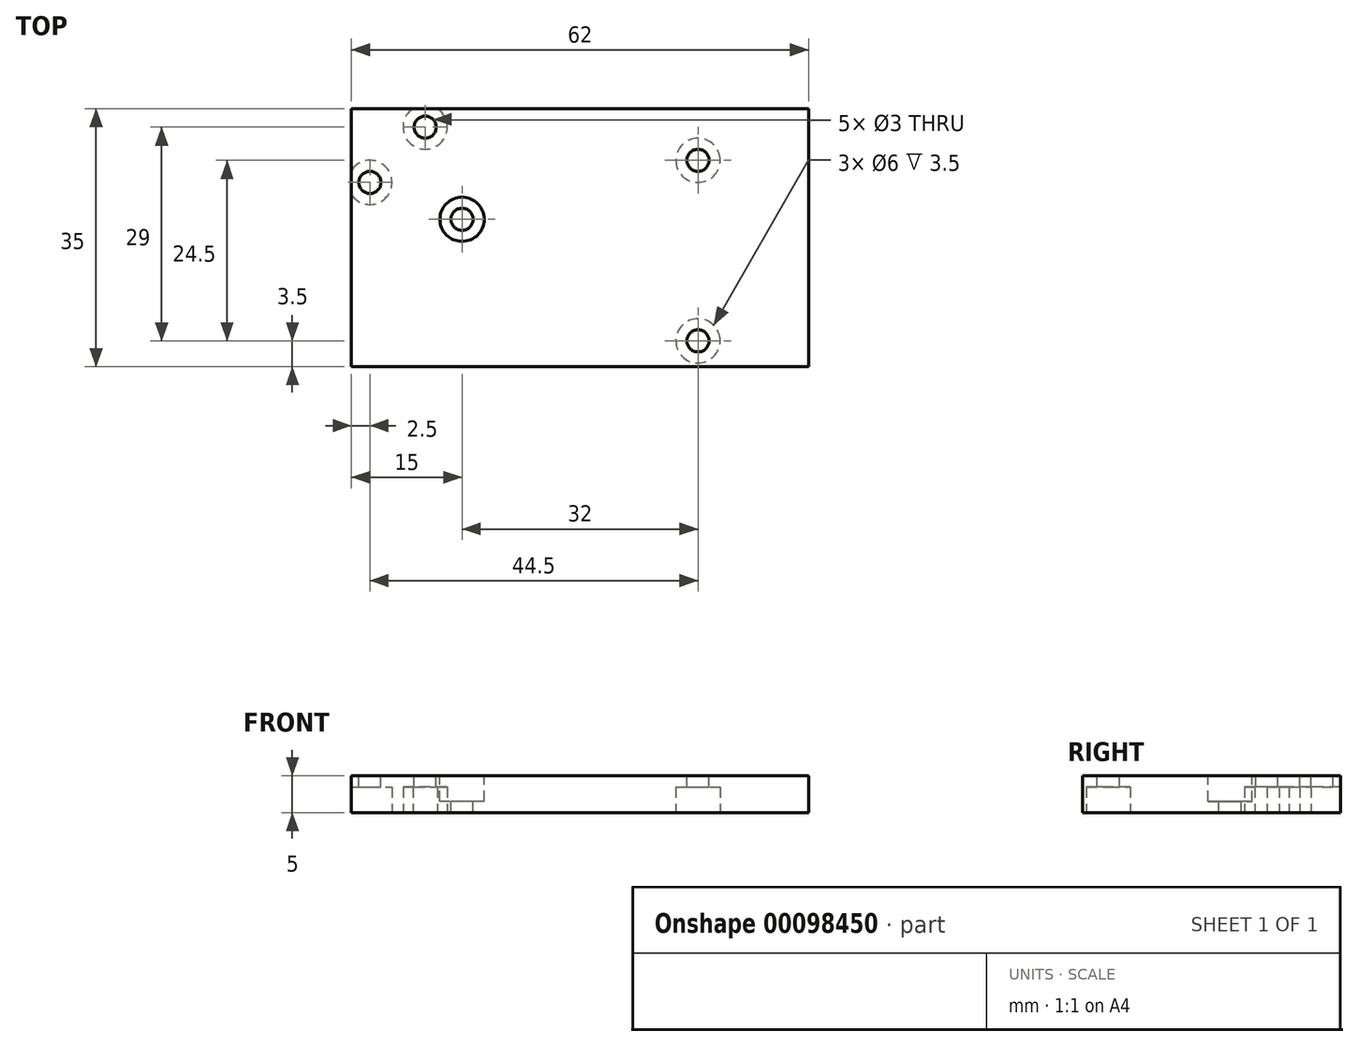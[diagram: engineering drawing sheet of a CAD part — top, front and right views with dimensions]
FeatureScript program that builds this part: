
annotation { "Feature Type Name" : "Feature", "Feature Type Description" : "" }
export const myFeature = defineFeature(function(context is Context, id is Id, definition is map)
    precondition{}
    {
        {
            var Q0;
            Q0=qCreatedBy(makeId("Top.planeOp"),FACE);
            var sketch = newSketch(context, id + "F0", { "sketchPlane" : qUnion([Q0])});
            skLineSegment(sketch, "E0.bottom", {"start": v(31, -17.5) * mm, "end": v(-31, -17.5) * mm});
            skLineSegment(sketch, "E0.top", {"start": v(31, 17.5) * mm, "end": v(-31, 17.5) * mm});
            skLineSegment(sketch, "E0.left", {"start": v(31, -17.5) * mm, "end": v(31, 17.5) * mm});
            skLineSegment(sketch, "E0.right", {"start": v(-31, -17.5) * mm, "end": v(-31, 17.5) * mm});
            skPoint(sketch, "E0.middle", {"position": v(0, 0) * mm});
            skSolve(sketch);
        }
        {
            var Q0;
            Q0=makeQuery(id+"F0.imprint","IMPRINT",FACE,{"disambiguationData":[TD([[makeQuery(id+"F0.imprint","IMPRINT",EDGE,{"derivedFrom":sQuery(id+"F0.wireOp",EDGE,"E0.bottom")}),-1.0]])]});
            extrude(context, id + "F1", {"entities" : qUnion([Q0]), "depth" : 5 * mm});
        }
        {
            var Q0;
            Q0=makeQuery(id+"F1.opExtrude","CAP_FACE",FACE,{"disambiguationData":[OSD([sQuery(id+"F0.wireOp",EDGE,"E0.bottom"),sQuery(id+"F0.wireOp",EDGE,"E0.top"),sQuery(id+"F0.wireOp",EDGE,"E0.left"),sQuery(id+"F0.wireOp",EDGE,"E0.right")])],"isStart":false});
            var sketch = newSketch(context, id + "F2", { "sketchPlane" : qUnion([Q0])});
            skCircle(sketch, "E1", {"center": v(-28.5, 7.5) * mm, "radius": 1.5 * mm});
            skCircle(sketch, "E2", {"center": v(-21, 15) * mm, "radius": 1.5 * mm});
            skSolve(sketch);
        }
        {
            var Q0;
            Q0 = qSketchRegion(id + "F2", true);
            extrude(context, id + "F3", {"entities" : qUnion([Q0]), "operationType" : NewBodyOperationType.REMOVE, "oppositeDirection" : true, "depth" : 5 * mm});
        }
        {
            var Q0;
            Q0=makeQuery(id+"F1.opExtrude","CAP_FACE",FACE,{"disambiguationData":[OSD([sQuery(id+"F0.wireOp",EDGE,"E0.bottom"),sQuery(id+"F0.wireOp",EDGE,"E0.top"),sQuery(id+"F0.wireOp",EDGE,"E0.left"),sQuery(id+"F0.wireOp",EDGE,"E0.right")])],"isStart":true});
            var sketch = newSketch(context, id + "F4", { "sketchPlane" : qUnion([Q0])});
            skCircle(sketch, "E3", {"center": v(-28.5, -7.5) * mm, "radius": 3 * mm});
            skCircle(sketch, "E4", {"center": v(-21, -15) * mm, "radius": 3 * mm});
            skSolve(sketch);
        }
        {
            var Q0;
            Q0 = qSketchRegion(id + "F4", true);
            extrude(context, id + "F5", {"entities" : qUnion([Q0]), "operationType" : NewBodyOperationType.REMOVE, "oppositeDirection" : true, "depth" : 3.5 * mm});
        }
        {
            var Q0;
            Q0=makeQuery(id+"F1.opExtrude","CAP_FACE",FACE,{"disambiguationData":[OSD([sQuery(id+"F0.wireOp",EDGE,"E0.bottom"),sQuery(id+"F0.wireOp",EDGE,"E0.top"),sQuery(id+"F0.wireOp",EDGE,"E0.left"),sQuery(id+"F0.wireOp",EDGE,"E0.right")])],"isStart":false});
            var sketch = newSketch(context, id + "F6", { "sketchPlane" : qUnion([Q0])});
            skCircle(sketch, "E5", {"center": v(-16, 2.5) * mm, "radius": 3 * mm});
            skSolve(sketch);
        }
        {
            var Q0;
            Q0=makeQuery(id+"F6.imprint","IMPRINT",FACE,{"disambiguationData":[TD([[makeQuery(id+"F6.imprint","IMPRINT",EDGE,{"derivedFrom":sQuery(id+"F6.wireOp",EDGE,"E5")}),1.0]])]});
            extrude(context, id + "F7", {"entities" : qUnion([Q0]), "operationType" : NewBodyOperationType.REMOVE, "oppositeDirection" : true, "depth" : 3.5 * mm});
        }
        {
            var Q0;
            Q0=makeQuery(id+"F7.boolean.opBoolean","COPY",FACE,{"derivedFrom":makeQuery(id+"F7.opExtrude","CAP_FACE",FACE,{"disambiguationData":[OSD([sQuery(id+"F6.wireOp",EDGE,"E5")])],"isStart":false})});
            var sketch = newSketch(context, id + "F8", { "sketchPlane" : qUnion([Q0])});
            skCircle(sketch, "E6", {"center": v(-16, 2.5) * mm, "radius": 1.5 * mm});
            skSolve(sketch);
        }
        {
            var Q0;
            Q0 = qSketchRegion(id + "F8", true);
            extrude(context, id + "F9", {"entities" : qUnion([Q0]), "operationType" : NewBodyOperationType.REMOVE, "oppositeDirection" : true, "depth" : 5 * mm});
        }
        {
            var Q0;
            Q0=makeQuery(id+"F1.opExtrude","CAP_FACE",FACE,{"disambiguationData":[OSD([sQuery(id+"F0.wireOp",EDGE,"E0.bottom"),sQuery(id+"F0.wireOp",EDGE,"E0.top"),sQuery(id+"F0.wireOp",EDGE,"E0.left"),sQuery(id+"F0.wireOp",EDGE,"E0.right")])],"isStart":false});
            var sketch = newSketch(context, id + "F10", { "sketchPlane" : qUnion([Q0])});
            skCircle(sketch, "E7", {"center": v(16, 10.5) * mm, "radius": 1.5 * mm});
            skCircle(sketch, "E8", {"center": v(16, -14) * mm, "radius": 1.5 * mm});
            skLineSegment(sketch, "E9", {"start": v(16, 10.5) * mm, "end": v(16, -14) * mm, "construction": true});
            skSolve(sketch);
        }
        {
            var Q0;
            Q0 = qSketchRegion(id + "F10", true);
            extrude(context, id + "F11", {"entities" : qUnion([Q0]), "operationType" : NewBodyOperationType.REMOVE, "oppositeDirection" : true, "depth" : 5 * mm});
        }
        {
            var Q0;
            Q0=makeQuery(id+"F1.opExtrude","CAP_FACE",FACE,{"disambiguationData":[OSD([sQuery(id+"F0.wireOp",EDGE,"E0.bottom"),sQuery(id+"F0.wireOp",EDGE,"E0.top"),sQuery(id+"F0.wireOp",EDGE,"E0.left"),sQuery(id+"F0.wireOp",EDGE,"E0.right")])],"isStart":true});
            var sketch = newSketch(context, id + "F12", { "sketchPlane" : qUnion([Q0])});
            skCircle(sketch, "E10", {"center": v(16, 14) * mm, "radius": 3 * mm});
            skCircle(sketch, "E11", {"center": v(16, -10.5) * mm, "radius": 3 * mm});
            skSolve(sketch);
        }
        {
            var Q0;
            Q0 = qSketchRegion(id + "F12", true);
            extrude(context, id + "F13", {"entities" : qUnion([Q0]), "operationType" : NewBodyOperationType.REMOVE, "oppositeDirection" : true, "depth" : 3.5 * mm});
        }
    });
